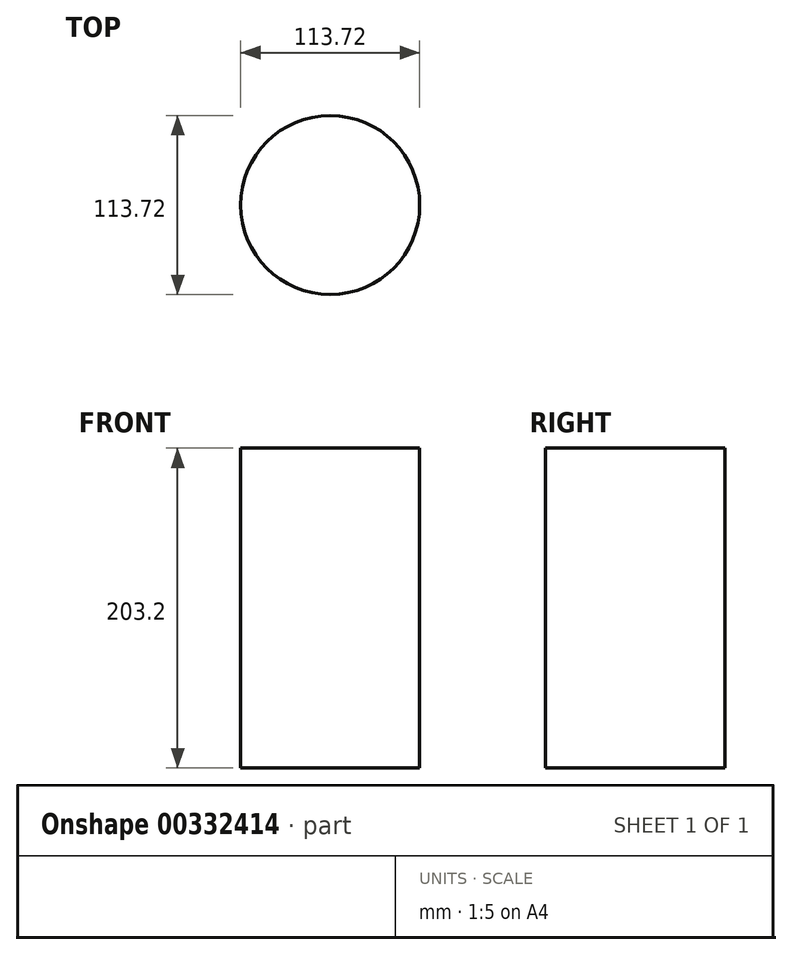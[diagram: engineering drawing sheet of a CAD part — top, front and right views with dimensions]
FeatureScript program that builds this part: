
annotation { "Feature Type Name" : "Feature", "Feature Type Description" : "" }
export const myFeature = defineFeature(function(context is Context, id is Id, definition is map)
    precondition{}
    {
        {
            var Q0;
            Q0=qCreatedBy(makeId("Top.planeOp"),FACE);
            var sketch = newSketch(context, id + "F0", { "sketchPlane" : qUnion([Q0])});
            skCircle(sketch, "E0", {"center": v(0, 0) * mm, "radius": 56.86 * mm});
            skSolve(sketch);
        }
        {
            var Q0;
            Q0=makeQuery(id+"F0.imprint","IMPRINT",FACE,{"disambiguationData":[TD([[makeQuery(id+"F0.imprint","IMPRINT",EDGE,{"derivedFrom":sQuery(id+"F0.wireOp",EDGE,"E0")}),1.0]])]});
            extrude(context, id + "F1", {"entities" : qUnion([Q0]), "endBound" : BoundingType.SYMMETRIC, "oppositeDirection" : true, "depth" : 203.2 * mm});
        }
    });
